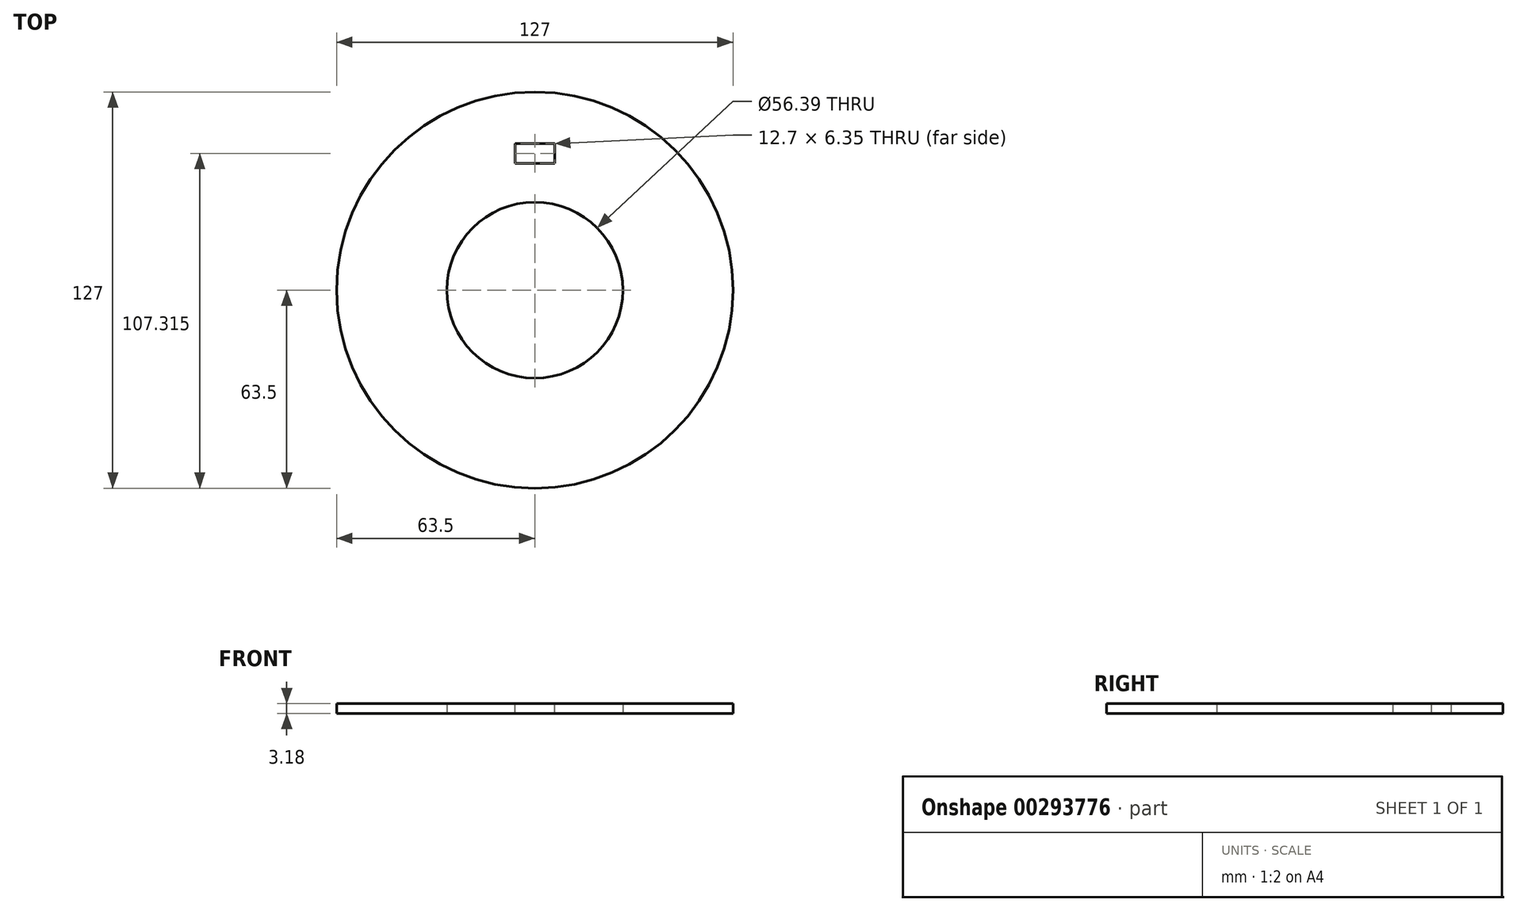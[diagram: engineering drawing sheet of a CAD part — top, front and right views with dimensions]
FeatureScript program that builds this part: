
annotation { "Feature Type Name" : "Feature", "Feature Type Description" : "" }
export const myFeature = defineFeature(function(context is Context, id is Id, definition is map)
    precondition{}
    {
        {
            var Q0;
            Q0=qCreatedBy(makeId("Top.planeOp"),FACE);
            var sketch = newSketch(context, id + "F0", { "sketchPlane" : qUnion([Q0])});
            skCircle(sketch, "E0", {"center": v(0, 0) * mm, "radius": 63.5 * mm});
            skCircle(sketch, "E1", {"center": v(0, 0) * mm, "radius": 28.2 * mm});
            skSolve(sketch);
        }
        {
            var Q0;
            Q0=makeQuery(id+"F0.imprint","IMPRINT",FACE,{"disambiguationData":[TD([[makeQuery(id+"F0.imprint","IMPRINT",EDGE,{"derivedFrom":sQuery(id+"F0.wireOp",EDGE,"E0")}),1.0]])]});
            var Q1;
            Q1 = qSketchRegion(id + "F0", true);
            extrude(context, id + "F1", {"entities" : qUnion([Q0, Q1]), "depth" : 3.17 * mm});
        }
        {
            var Q0;
            Q0=makeQuery(id+"F1.opExtrude","CAP_FACE",FACE,{"disambiguationData":[OSD([sQuery(id+"F0.wireOp",EDGE,"E0"),sQuery(id+"F0.wireOp",EDGE,"E1")])],"isStart":false});
            var sketch = newSketch(context, id + "F2", { "sketchPlane" : qUnion([Q0])});
            skLineSegment(sketch, "E2.bottom", {"start": v(-6.35, 47) * mm, "end": v(6.35, 47) * mm});
            skLineSegment(sketch, "E2.top", {"start": v(-6.35, 40.64) * mm, "end": v(6.35, 40.64) * mm});
            skLineSegment(sketch, "E2.left", {"start": v(-6.35, 47) * mm, "end": v(-6.35, 40.64) * mm});
            skLineSegment(sketch, "E2.right", {"start": v(6.35, 47) * mm, "end": v(6.35, 40.64) * mm});
            skCircle(sketch, "E3", {"center": v(0, 0) * mm, "radius": 50.8 * mm, "construction": true});
            skPoint(sketch, "E4.middle", {"position": v(0, 40.38) * mm});
            skSolve(sketch);
        }
        {
            var Q0;
            Q0 = qSketchRegion(id + "F2", true);
            extrude(context, id + "F3", {"entities" : qUnion([Q0]), "operationType" : NewBodyOperationType.REMOVE, "endBound" : BoundingType.THROUGH_ALL, "oppositeDirection" : true, "depth" : 25.4 * mm});
        }
    });
